# Revit family: O13591001_Lavamanos Varese
name_source: partatom
category: Plumbing Fixtures
units: mm (PartAtom-declared; Revit-internal decimal feet)

## family parameters
Cut with Voids When Loaded = No
Host = Face
OmniClass Number = 23.31.13.11
OmniClass Title = Single Sinks
Part Type = Normal
Room Calculation Point = No
Round Connector Dimension = Use Diameter
Shared = No

## types (1)
- O13591001_Lavamanos Varese
    Agujeros para Griferia = N.A
    Alto = 140 mm  [stored 0.459318 ft]
    Ancho = 375 mm  [stored 1.23031 ft]
    Creado por = BIMBAU
    Default Elevation = 1219 mm
    Description = El lavamanos Varese tipo vessel rectangular está elaborado en porcelana sanitaria y cuenta con diseño contemporáneo, inspirado en formas clásicas para darle a tu baño el mejor estilo.
    Fecha de creación = 07/04/2021
    Forma = Rectangular
    Garantía = Garantia integral de por vida
    Línea = Varese
    Manufacturer = Corona
    Material = Corona_Porcelana_Sanitaria
    Material 2 = Corona_Acero inoxidable
    Model = Varese
    Normatividad = ASME / ANSI A112.19.2
    Peso Neto aprox = 33.2 lbs (15.1 kg)
    Pozo = 37.5 x 35 cm x 12.7 cm
    Productos Compatibles = Grifería monocontrol alta Grifería 8 pulgadas a pared
    Profundidad = 385 mm  [stored 1.26312 ft]
    Referencia = O13591001
    Resistencia al rayado = Alta resistencia al rayado y cambios de temperatura
    URL = https://corona.co
    Uso = Residencial

note: [stored X ft] marks values corroborated as IEEE doubles in the binary element streams (Revit-internal decimal feet)

## geometry (parser evidence)
native form markers: Sweep x7
no freeform markers — native parametric forms only
